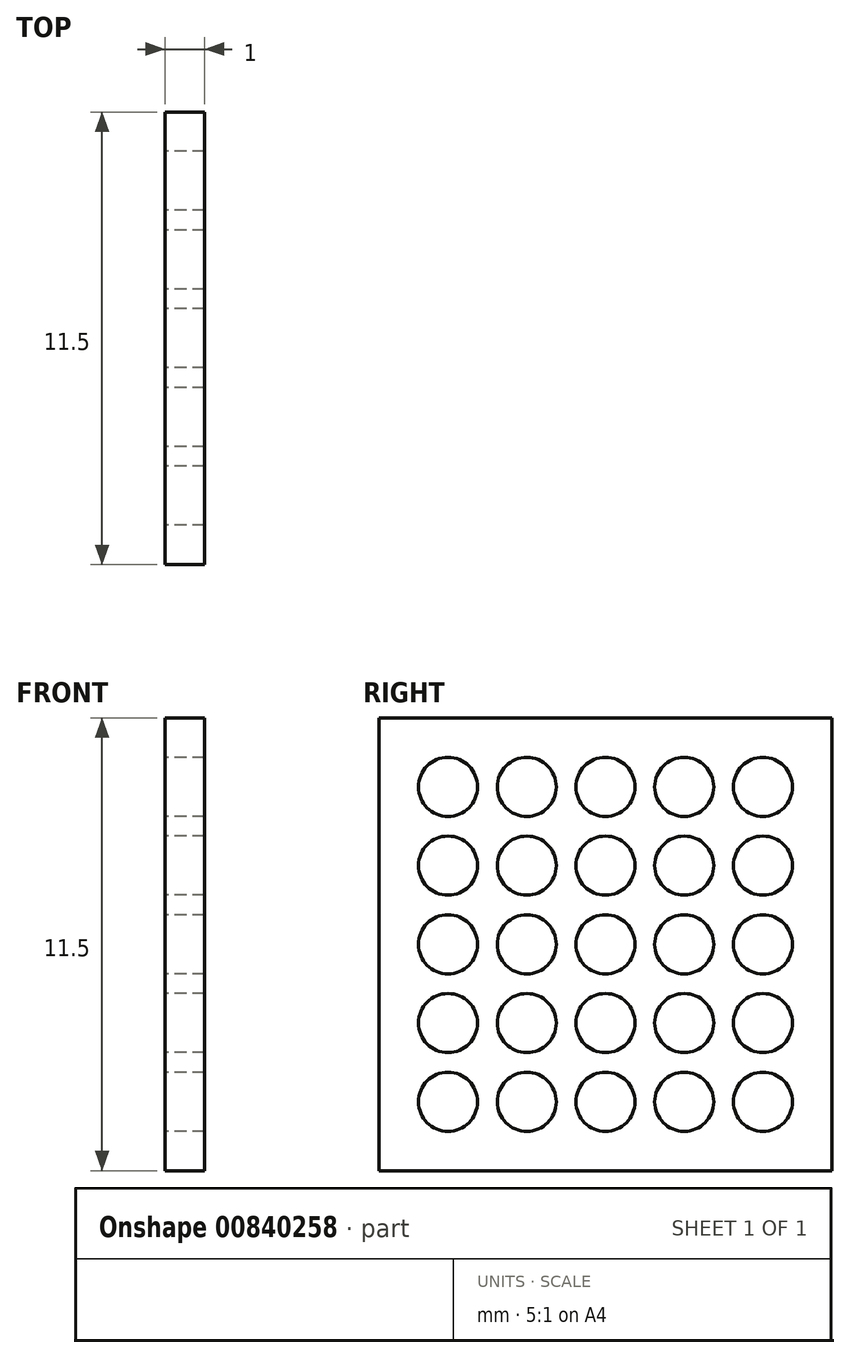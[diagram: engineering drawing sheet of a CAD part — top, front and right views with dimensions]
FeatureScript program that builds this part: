
annotation { "Feature Type Name" : "Feature", "Feature Type Description" : "" }
export const myFeature = defineFeature(function(context is Context, id is Id, definition is map)
    precondition{}
    {
        {
            var Q0;
            Q0=qCreatedBy(makeId("Right.planeOp"),FACE);
            var sketch = newSketch(context, id + "F0", { "sketchPlane" : qUnion([Q0])});
            skLineSegment(sketch, "E0.bottom", {"start": v(0, 0) * mm, "end": v(8.38, 0) * mm});
            skLineSegment(sketch, "E0.top", {"start": v(0, -11.5) * mm, "end": v(11.5, -11.5) * mm});
            skLineSegment(sketch, "E0.left", {"start": v(0, 0) * mm, "end": v(0, -11.5) * mm});
            skCircle(sketch, "E1", {"center": v(5.75, -5.75) * mm, "radius": 0.75 * mm});
            skLineSegment(sketch, "E2", {"start": v(11.5, 0) * mm, "end": v(11.5, -11.5) * mm});
            skCircle(sketch, "E3", {"center": v(5.75, -3.75) * mm, "radius": 0.75 * mm});
            skCircle(sketch, "E4", {"center": v(5.75, -1.75) * mm, "radius": 0.75 * mm});
            skCircle(sketch, "E5", {"center": v(3.75, -5.75) * mm, "radius": 0.75 * mm});
            skCircle(sketch, "E6", {"center": v(1.75, -5.75) * mm, "radius": 0.75 * mm});
            skCircle(sketch, "E7.MirrorC", {"center": v(1.75, -1.75) * mm, "radius": 0.75 * mm});
            skCircle(sketch, "E8.MirrorC", {"center": v(3.75, -1.75) * mm, "radius": 0.75 * mm});
            skCircle(sketch, "E9.MirrorC", {"center": v(1.75, -3.75) * mm, "radius": 0.75 * mm});
            skCircle(sketch, "E10", {"center": v(3.75, -3.75) * mm, "radius": 0.75 * mm});
            skCircle(sketch, "E11.MirrorC", {"center": v(7.75, -1.75) * mm, "radius": 0.75 * mm});
            skCircle(sketch, "E12.MirrorC", {"center": v(9.75, -1.75) * mm, "radius": 0.75 * mm});
            skCircle(sketch, "E13.MirrorC", {"center": v(9.75, -3.75) * mm, "radius": 0.75 * mm});
            skCircle(sketch, "E14.MirrorC", {"center": v(7.75, -3.75) * mm, "radius": 0.75 * mm});
            skCircle(sketch, "E15.MirrorC", {"center": v(7.75, -5.75) * mm, "radius": 0.75 * mm});
            skCircle(sketch, "E16.MirrorC", {"center": v(9.75, -5.75) * mm, "radius": 0.75 * mm});
            skCircle(sketch, "E17.MirrorC", {"center": v(1.75, -9.75) * mm, "radius": 0.75 * mm});
            skCircle(sketch, "E18.MirrorC", {"center": v(1.75, -7.75) * mm, "radius": 0.75 * mm});
            skCircle(sketch, "E19.MirrorC", {"center": v(3.75, -7.75) * mm, "radius": 0.75 * mm});
            skCircle(sketch, "E20.MirrorC", {"center": v(3.75, -9.75) * mm, "radius": 0.75 * mm});
            skCircle(sketch, "E21.MirrorC", {"center": v(7.75, -9.75) * mm, "radius": 0.75 * mm});
            skCircle(sketch, "E22.MirrorC", {"center": v(7.75, -7.75) * mm, "radius": 0.75 * mm});
            skCircle(sketch, "E23.MirrorC", {"center": v(9.75, -9.75) * mm, "radius": 0.75 * mm});
            skCircle(sketch, "E24.MirrorC", {"center": v(9.75, -7.75) * mm, "radius": 0.75 * mm});
            skCircle(sketch, "E25.MirrorC", {"center": v(5.75, -7.75) * mm, "radius": 0.75 * mm});
            skCircle(sketch, "E26.MirrorC", {"center": v(5.75, -9.75) * mm, "radius": 0.75 * mm});
            skLineSegment(sketch, "E27", {"start": v(9.5, 0) * mm, "end": v(8.38, 0) * mm});
            skLineSegment(sketch, "E28", {"start": v(11.5, 0) * mm, "end": v(10.38, 0) * mm});
            skLineSegment(sketch, "E29", {"start": v(10.38, 0) * mm, "end": v(10.38, 10) * mm});
            skLineSegment(sketch, "E30", {"start": v(10.38, 10) * mm, "end": v(8.38, 10) * mm});
            skLineSegment(sketch, "E31", {"start": v(8.38, 10) * mm, "end": v(8.38, 0) * mm});
            skLineSegment(sketch, "E32", {"start": v(8.38, 0) * mm, "end": v(10.38, 0) * mm});
            skSolve(sketch);
        }
        {
            var Q0;
            Q0=makeQuery(id+"F0.imprint","IMPRINT",FACE,{"disambiguationData":[TD([[makeQuery(id+"F0.imprint","IMPRINT",EDGE,{"derivedFrom":sQuery(id+"F0.wireOp",EDGE,"E0.bottom")}),-1.0]])]});
            var Q1;
            Q1=makeQuery(id+"F0.imprint","IMPRINT",FACE,{"disambiguationData":[TD([[makeQuery(id+"F0.imprint","IMPRINT",EDGE,{"derivedFrom":sQuery(id+"F0.wireOp",EDGE,"r65wuaeR-pUGk-UfhY-v5oq-7bkjaNJfQmKm.bottom")}),-1.0]])]});
            var Q2;
            Q2=makeQuery(id+"F0.imprint","IMPRINT",FACE,{"disambiguationData":[TD([[makeQuery(id+"F0.imprint","IMPRINT",EDGE,{"derivedFrom":sQuery(id+"F0.wireOp",EDGE,"n5EaUuf3-CoM6-EQkv-XzT1-ydr3onYee1LO.bottom")}),1.0]])]});
            var Q3;
            Q3=makeQuery(id+"F0.imprint","IMPRINT",FACE,{"disambiguationData":[TD([[makeQuery(id+"F0.imprint","IMPRINT",EDGE,{"derivedFrom":sQuery(id+"F0.wireOp",EDGE,"2NUbogVr-x7fL-9LVX-WR3f-6RiyyzUn8nbi.bottom")}),-1.0]])]});
            extrude(context, id + "F1", {"entities" : qUnion([Q0, Q1, Q2, Q3]), "depth" : 1 * mm, "offsetDistance" : 25 * mm});
        }
    });
